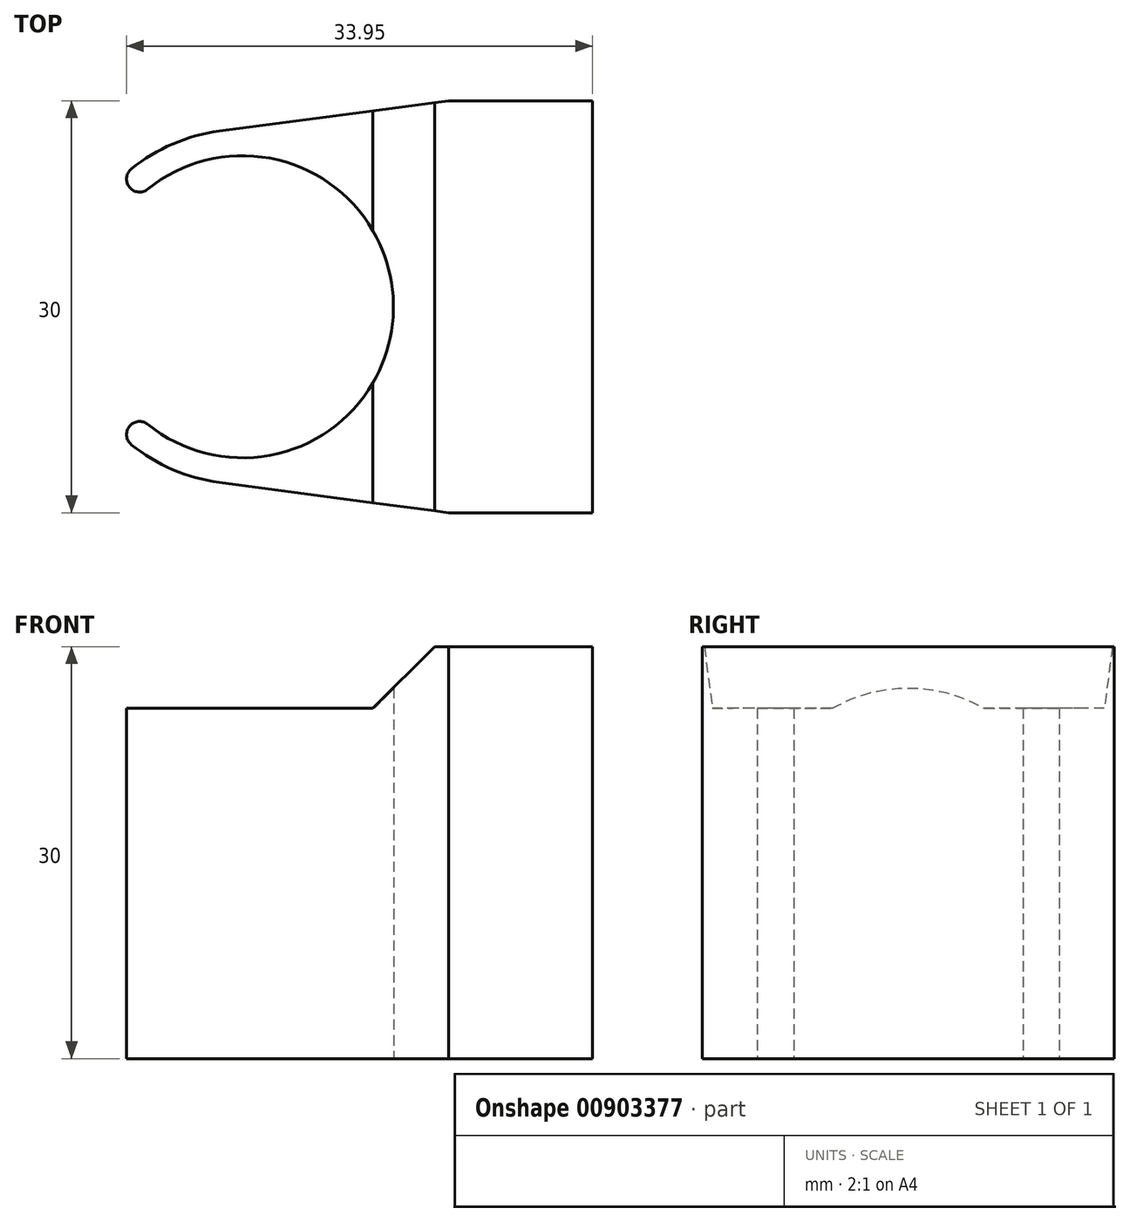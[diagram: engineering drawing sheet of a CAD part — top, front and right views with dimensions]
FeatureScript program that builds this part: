
annotation { "Feature Type Name" : "Feature", "Feature Type Description" : "" }
export const myFeature = defineFeature(function(context is Context, id is Id, definition is map)
    precondition{}
    {
        {
            var Q0;
            Q0=qCreatedBy(makeId("Top.planeOp"),FACE);
            var sketch = newSketch(context, id + "F0", { "sketchPlane" : qUnion([Q0])});
            skLineSegment(sketch, "E0", {"start": v(0, 0) * mm, "end": v(10.5, 0) * mm});
            skLineSegment(sketch, "E1", {"start": v(10.5, 0) * mm, "end": v(10.5, 30) * mm});
            skLineSegment(sketch, "E2", {"start": v(10.5, 30) * mm, "end": v(0, 30) * mm});
            skLineSegment(sketch, "E3", {"start": v(10.5, 15) * mm, "end": v(-15, 15) * mm, "construction": true});
            skLineSegment(sketch, "E4", {"start": v(0, 30) * mm, "end": v(0, 0) * mm, "construction": true});
            skPoint(sketch, "E5", {"position": v(-4, 15) * mm});
            skArc(sketch, "E6", {"start": v(-16.7, 27.79) * mm, "mid": v(-20.08, 26.86) * mm, "end": v(-23.1, 25.04) * mm});
            skLineSegment(sketch, "E7", {"start": v(0, 30) * mm, "end": v(-16.7, 27.79) * mm});
            skArc(sketch, "E8", {"start": v(-4, 15) * mm, "mid": v(-10.25, 24.92) * mm, "end": v(-21.9, 23.56) * mm});
            skArc(sketch, "E9", {"start": v(-23.1, 25.04) * mm, "mid": v(-23.24, 23.7) * mm, "end": v(-21.9, 23.56) * mm});
            skLineSegment(sketch, "E10.MirrorCS", {"start": v(0, 0) * mm, "end": v(-16.7, 2.21) * mm});
            skArc(sketch, "E11.MirrorCS", {"start": v(-16.7, 2.21) * mm, "mid": v(-20.08, 3.14) * mm, "end": v(-23.1, 4.96) * mm});
            skArc(sketch, "E12.MirrorCS", {"start": v(-23.1, 4.96) * mm, "mid": v(-23.24, 6.3) * mm, "end": v(-21.9, 6.44) * mm});
            skArc(sketch, "E13.MirrorCS", {"start": v(-4, 15) * mm, "mid": v(-10.25, 5.08) * mm, "end": v(-21.9, 6.44) * mm});
            skSolve(sketch);
        }
        {
            var Q0;
            Q0 = qSketchRegion(id + "F0", true);
            extrude(context, id + "F1", {"entities" : qUnion([Q0]), "depth" : 30 * mm, "offsetDistance" : 25 * mm});
        }
        {
            var Q0;
            Q0=makeQuery(id+"F1.opExtrude","SWEPT_FACE",FACE,{"disambiguationData":[OSD([sQuery(id+"F0.wireOp",EDGE,"E0")])]});
            var sketch = newSketch(context, id + "F2", { "sketchPlane" : qUnion([Q0])});
            skLineSegment(sketch, "E14", {"start": v(-26.56, 36) * mm, "end": v(0, 36) * mm});
            skLineSegment(sketch, "E15", {"start": v(0, 36) * mm, "end": v(0, 30) * mm});
            skLineSegment(sketch, "E16", {"start": v(0, 30) * mm, "end": v(-1, 30) * mm});
            skLineSegment(sketch, "E17", {"start": v(-1, 30) * mm, "end": v(-5.5, 25.5) * mm});
            skLineSegment(sketch, "E18", {"start": v(-5.5, 25.5) * mm, "end": v(-26.56, 25.5) * mm});
            skLineSegment(sketch, "E19", {"start": v(-26.56, 25.5) * mm, "end": v(-26.56, 36) * mm});
            skSolve(sketch);
        }
        {
            var Q0;
            Q0 = qSketchRegion(id + "F2", true);
            extrude(context, id + "F3", {"entities" : qUnion([Q0]), "operationType" : NewBodyOperationType.REMOVE, "oppositeDirection" : true, "depth" : 40 * mm, "offsetDistance" : 25 * mm});
        }
    });
